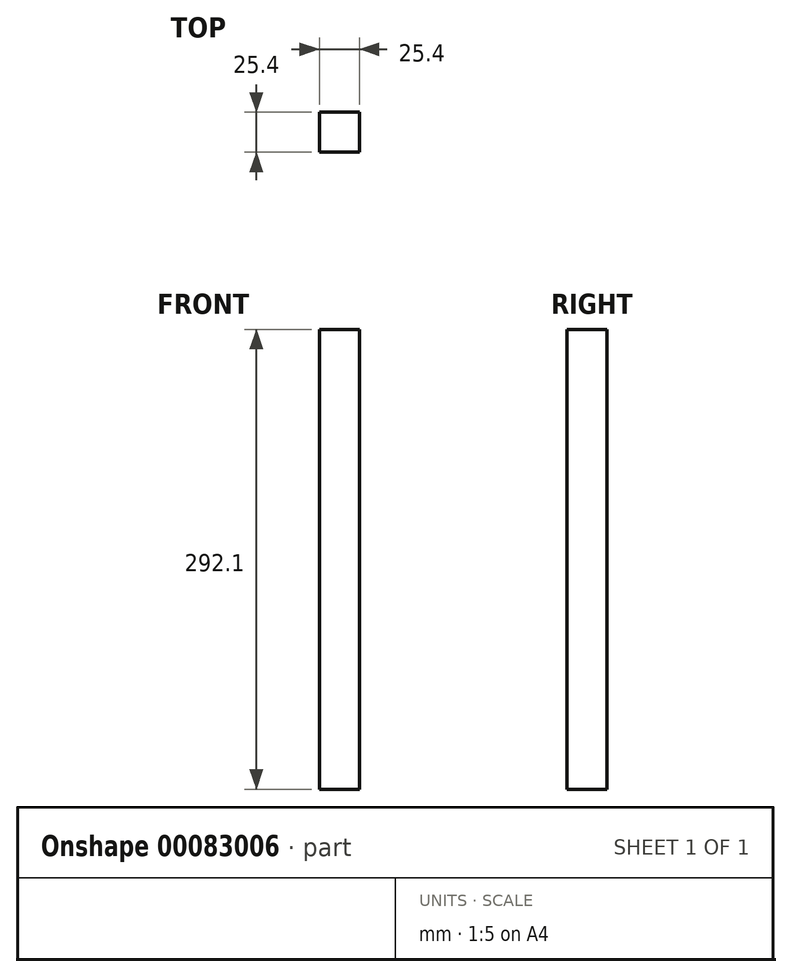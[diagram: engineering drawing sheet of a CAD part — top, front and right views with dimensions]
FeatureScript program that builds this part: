
annotation { "Feature Type Name" : "Feature", "Feature Type Description" : "" }
export const myFeature = defineFeature(function(context is Context, id is Id, definition is map)
    precondition{}
    {
        {
            var Q0;
            Q0=qCreatedBy(makeId("Top.planeOp"),FACE);
            var sketch = newSketch(context, id + "F0", { "sketchPlane" : qUnion([Q0])});
            skLineSegment(sketch, "E0.bottom", {"start": v(-95.13, 31.98) * mm, "end": v(-69.73, 31.98) * mm});
            skLineSegment(sketch, "E0.top", {"start": v(-95.13, 6.58) * mm, "end": v(-69.73, 6.58) * mm});
            skLineSegment(sketch, "E0.left", {"start": v(-95.13, 31.98) * mm, "end": v(-95.13, 6.58) * mm});
            skLineSegment(sketch, "E0.right", {"start": v(-69.73, 31.98) * mm, "end": v(-69.73, 6.58) * mm});
            skSolve(sketch);
        }
        {
            var Q0;
            Q0=makeQuery(id+"F0.imprint","IMPRINT",FACE,{"disambiguationData":[TD([[makeQuery(id+"F0.imprint","IMPRINT",EDGE,{"derivedFrom":sQuery(id+"F0.wireOp",EDGE,"E0.bottom")}),-1.0]])]});
            extrude(context, id + "F1", {"entities" : qUnion([Q0]), "depth" : 292.1 * mm});
        }
    });
